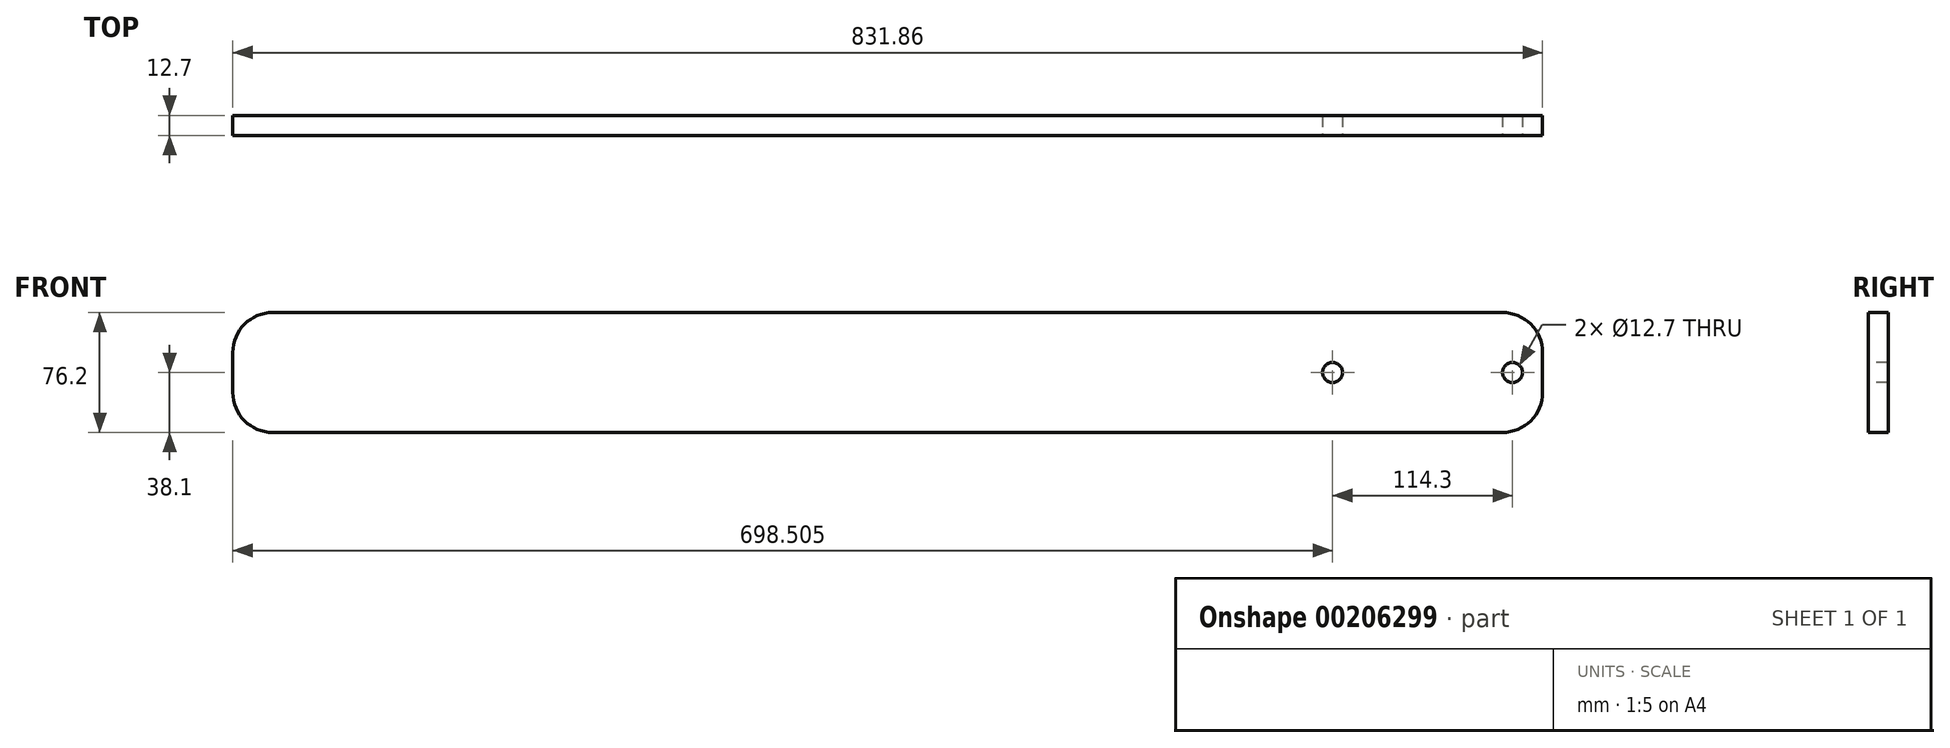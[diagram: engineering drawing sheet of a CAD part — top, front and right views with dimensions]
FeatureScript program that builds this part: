
annotation { "Feature Type Name" : "Feature", "Feature Type Description" : "" }
export const myFeature = defineFeature(function(context is Context, id is Id, definition is map)
    precondition{}
    {
        {
            var Q0;
            Q0=qCreatedBy(makeId("Front.planeOp"),FACE);
            var sketch = newSketch(context, id + "F0", { "sketchPlane" : qUnion([Q0])});
            skLineSegment(sketch, "E0.bottom", {"start": v(-415.93, 38.1) * mm, "end": v(415.93, 38.1) * mm});
            skLineSegment(sketch, "E0.top", {"start": v(-415.93, -38.1) * mm, "end": v(415.93, -38.1) * mm});
            skLineSegment(sketch, "E0.left", {"start": v(-415.93, 38.1) * mm, "end": v(-415.93, -38.1) * mm});
            skLineSegment(sketch, "E0.right", {"start": v(415.93, 38.1) * mm, "end": v(415.93, -38.1) * mm});
            skPoint(sketch, "E0.middle", {"position": v(0, 0) * mm});
            skSolve(sketch);
        }
        {
            var Q0;
            Q0 = qSketchRegion(id + "F0", true);
            extrude(context, id + "F1", {"entities" : qUnion([Q0]), "endBound" : BoundingType.SYMMETRIC, "depth" : 12.7 * mm});
        }
        {
            var Q0;
            Q0=makeQuery(id+"F1.opExtrude","CAP_FACE",FACE,{"disambiguationData":[OSD([sQuery(id+"F0.wireOp",EDGE,"E0.bottom"),sQuery(id+"F0.wireOp",EDGE,"E0.top"),sQuery(id+"F0.wireOp",EDGE,"E0.left"),sQuery(id+"F0.wireOp",EDGE,"E0.right")])],"isStart":false});
            var sketch = newSketch(context, id + "F2", { "sketchPlane" : qUnion([Q0])});
            skLineSegment(sketch, "E1", {"start": v(-415.93, 0) * mm, "end": v(415.93, 0) * mm, "construction": true});
            skCircle(sketch, "E2", {"center": v(282.58, 0) * mm, "radius": 6.35 * mm});
            skCircle(sketch, "E3", {"center": v(396.88, 0) * mm, "radius": 6.35 * mm});
            skSolve(sketch);
        }
        {
            var Q0;
            Q0 = qSketchRegion(id + "F2", true);
            extrude(context, id + "F3", {"entities" : qUnion([Q0]), "operationType" : NewBodyOperationType.REMOVE, "oppositeDirection" : true, "depth" : 25.4 * mm});
        }
        {
            var Q0;
            Q0=makeQuery(id+"F1.opExtrude","SWEPT_EDGE",EDGE,{"disambiguationData":[OSD([sQuery(id+"F0.wireOp",EDGE,"E0.bottom"),sQuery(id+"F0.wireOp",EDGE,"E0.left")])]});
            var Q1;
            Q1=makeQuery(id+"F1.opExtrude","SWEPT_EDGE",EDGE,{"disambiguationData":[OSD([sQuery(id+"F0.wireOp",EDGE,"E0.top"),sQuery(id+"F0.wireOp",EDGE,"E0.left")])]});
            var Q2;
            Q2=makeQuery(id+"F1.opExtrude","SWEPT_EDGE",EDGE,{"disambiguationData":[OSD([sQuery(id+"F0.wireOp",EDGE,"E0.top"),sQuery(id+"F0.wireOp",EDGE,"E0.right")])]});
            var Q3;
            Q3=makeQuery(id+"F1.opExtrude","SWEPT_EDGE",EDGE,{"disambiguationData":[OSD([sQuery(id+"F0.wireOp",EDGE,"E0.bottom"),sQuery(id+"F0.wireOp",EDGE,"E0.right")])]});
            fillet(context, id + "F4", {"entities" : qUnion([Q0, Q1, Q2, Q3]), "radius" : 25.4 * mm, "tangentPropagation" : true, "allowEdgeOverflow" : false});
        }
    });
